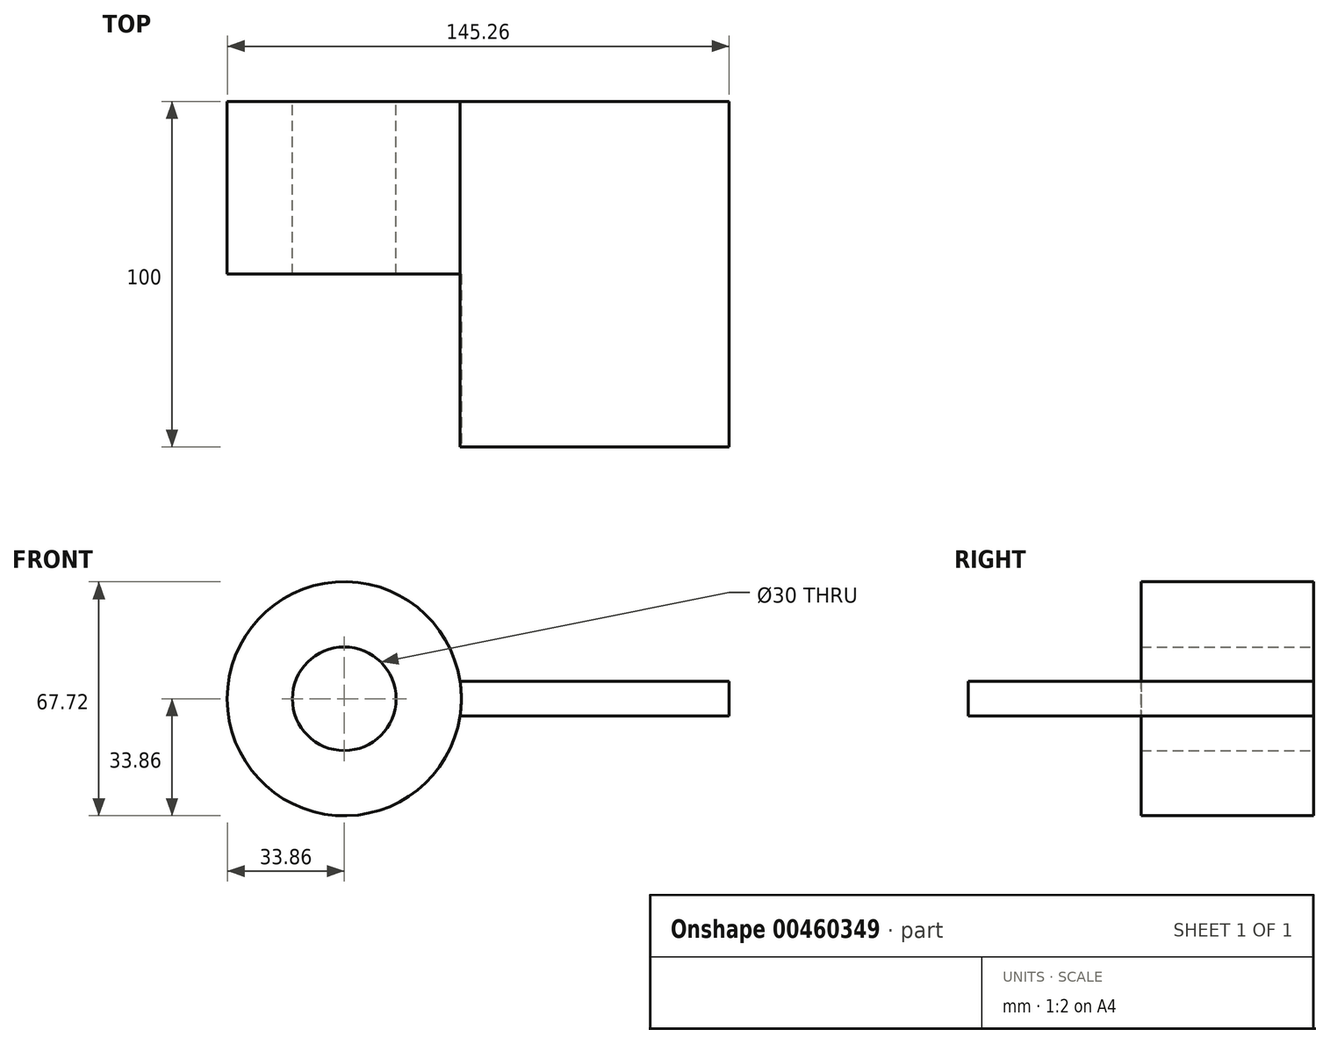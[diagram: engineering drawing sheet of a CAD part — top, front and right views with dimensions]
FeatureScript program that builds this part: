
annotation { "Feature Type Name" : "Feature", "Feature Type Description" : "" }
export const myFeature = defineFeature(function(context is Context, id is Id, definition is map)
    precondition{}
    {
        {
            var Q0;
            Q0=qCreatedBy(makeId("Top.planeOp"),FACE);
            var sketch = newSketch(context, id + "F0", { "sketchPlane" : qUnion([Q0])});
            skLineSegment(sketch, "E0.bottom", {"start": v(-33.86, 100) * mm, "end": v(-15, 100) * mm});
            skLineSegment(sketch, "E0.top", {"start": v(-33.86, 50) * mm, "end": v(-15, 50) * mm});
            skLineSegment(sketch, "E0.left", {"start": v(-33.86, 100) * mm, "end": v(-33.86, 50) * mm});
            skLineSegment(sketch, "E0.right", {"start": v(-15, 100) * mm, "end": v(-15, 50) * mm});
            skLineSegment(sketch, "E1", {"start": v(0, 49.86) * mm, "end": v(0, 18.53) * mm});
            skSolve(sketch);
        }
        {
            var Q0;
            Q0 = qSketchRegion(id + "F0", true);
            var Q1;
            Q1=sQuery(id+"F0.wireOp",EDGE,"E1");
            revolve(context, id + "F1", {"entities" : qUnion([Q0]), "axis" : qUnion([Q1]), "revolveType" : RevolveType.FULL});
        }
        {
            var Q0;
            Q0=qCreatedBy(makeId("Front.planeOp"),FACE);
            var sketch = newSketch(context, id + "F2", { "sketchPlane" : qUnion([Q0])});
            skLineSegment(sketch, "E2", {"start": v(33.5, 5) * mm, "end": v(111.4, 5) * mm});
            skLineSegment(sketch, "E3", {"start": v(111.4, 5) * mm, "end": v(111.4, -5) * mm});
            skLineSegment(sketch, "E4", {"start": v(111.4, -5) * mm, "end": v(33.5, -5) * mm});
            skLineSegment(sketch, "E5", {"start": v(0, 0) * mm, "end": v(111.4, 0) * mm, "construction": true});
            skArc(sketch, "E6.0", {"start": v(33.5, -5) * mm, "mid": v(33.86, 0) * mm, "end": v(33.5, 5) * mm});
            skSolve(sketch);
        }
        {
            var Q0;
            Q0=makeQuery(id+"F2.imprint","IMPRINT",FACE,{"disambiguationData":[TD([[makeQuery(id+"F2.imprint","IMPRINT",EDGE,{"derivedFrom":sQuery(id+"F2.wireOp",EDGE,"E2")}),-1.0]])]});
            extrude(context, id + "F3", {"entities" : qUnion([Q0]), "operationType" : NewBodyOperationType.ADD, "oppositeDirection" : true, "depth" : 100 * mm});
        }
    });
